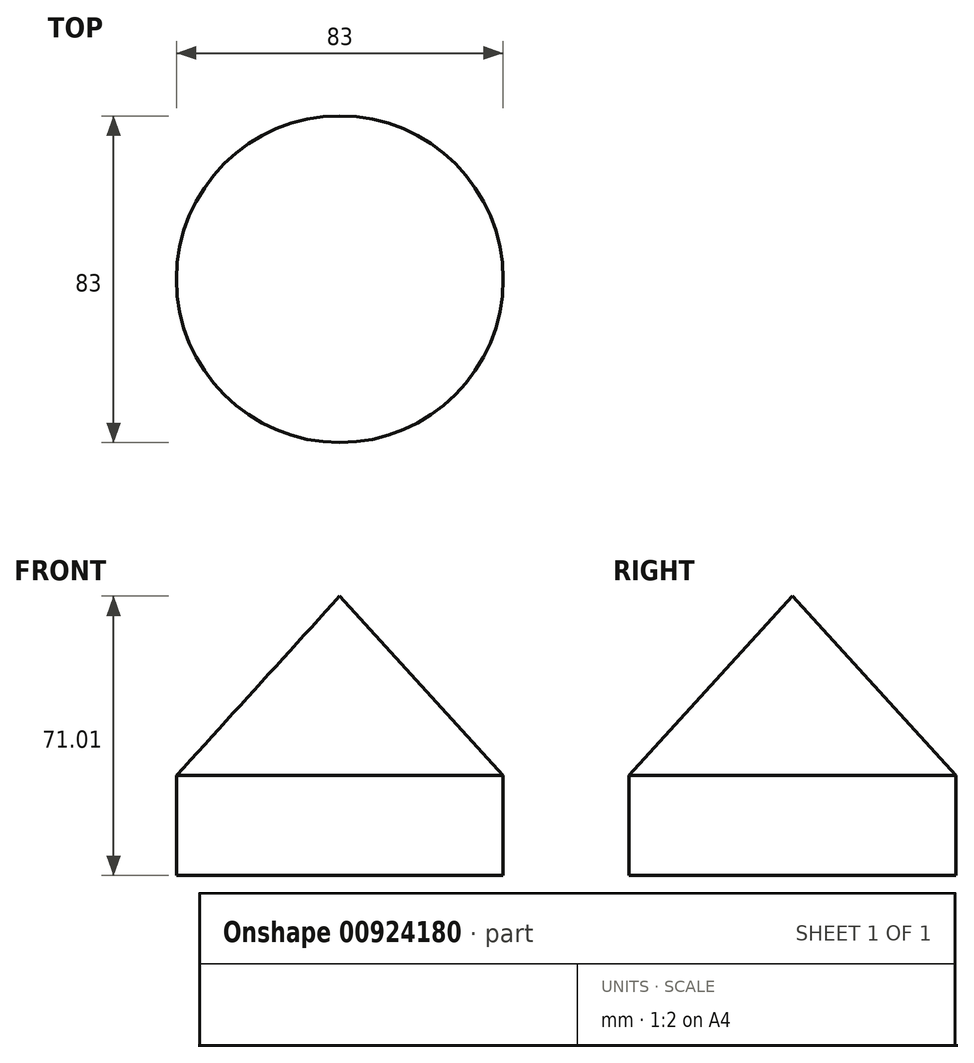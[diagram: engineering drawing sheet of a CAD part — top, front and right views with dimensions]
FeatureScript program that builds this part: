
annotation { "Feature Type Name" : "Feature", "Feature Type Description" : "" }
export const myFeature = defineFeature(function(context is Context, id is Id, definition is map)
    precondition{}
    {
        {
            var Q0;
            Q0=qCreatedBy(makeId("Top.planeOp"),FACE);
            var sketch = newSketch(context, id + "F0", { "sketchPlane" : qUnion([Q0])});
            skCircle(sketch, "E0", {"center": v(0, 0) * mm, "radius": 41.5 * mm});
            skSolve(sketch);
        }
        {
            var Q0;
            Q0=makeQuery(id+"F0.imprint","IMPRINT",FACE,{"disambiguationData":[TD([[makeQuery(id+"F0.imprint","IMPRINT",EDGE,{"derivedFrom":sQuery(id+"F0.wireOp",EDGE,"E0")}),1.0]])]});
            extrude(context, id + "F1", {"entities" : qUnion([Q0]), "depth" : 25.4 * mm, "offsetDistance" : 25.4 * mm});
        }
        {
            var Q0;
            Q0=qCreatedBy(makeId("Front.planeOp"),FACE);
            var sketch = newSketch(context, id + "F2", { "sketchPlane" : qUnion([Q0])});
            skLineSegment(sketch, "E1.0", {"start": v(-41.5, 25.4) * mm, "end": v(41.5, 25.4) * mm, "construction": true});
            skLineSegment(sketch, "E2", {"start": v(0, 71.01) * mm, "end": v(41.5, 25.4) * mm});
            skPoint(sketch, "E2.startSnap0", {"position": v(0, 25.4) * mm});
            skLineSegment(sketch, "E3", {"start": v(0, 71.01) * mm, "end": v(0, 25.4) * mm});
            skLineSegment(sketch, "E4", {"start": v(0, 25.4) * mm, "end": v(41.5, 25.4) * mm});
            skSolve(sketch);
        }
        {
            var Q0;
            Q0=makeQuery(id+"F2.imprint","IMPRINT",FACE,{"disambiguationData":[TD([[makeQuery(id+"F2.imprint","IMPRINT",EDGE,{"derivedFrom":sQuery(id+"F2.wireOp",EDGE,"E2")}),-1.0]])]});
            var Q1;
            Q1=sQuery(id+"F2.wireOp",EDGE,"E3");
            revolve(context, id + "F3", {"operationType" : NewBodyOperationType.ADD, "surfaceOperationType" : NewSurfaceOperationType.NEW, "entities" : qUnion([Q0]), "axis" : qUnion([Q1]), "revolveType" : RevolveType.FULL});
        }
    });
